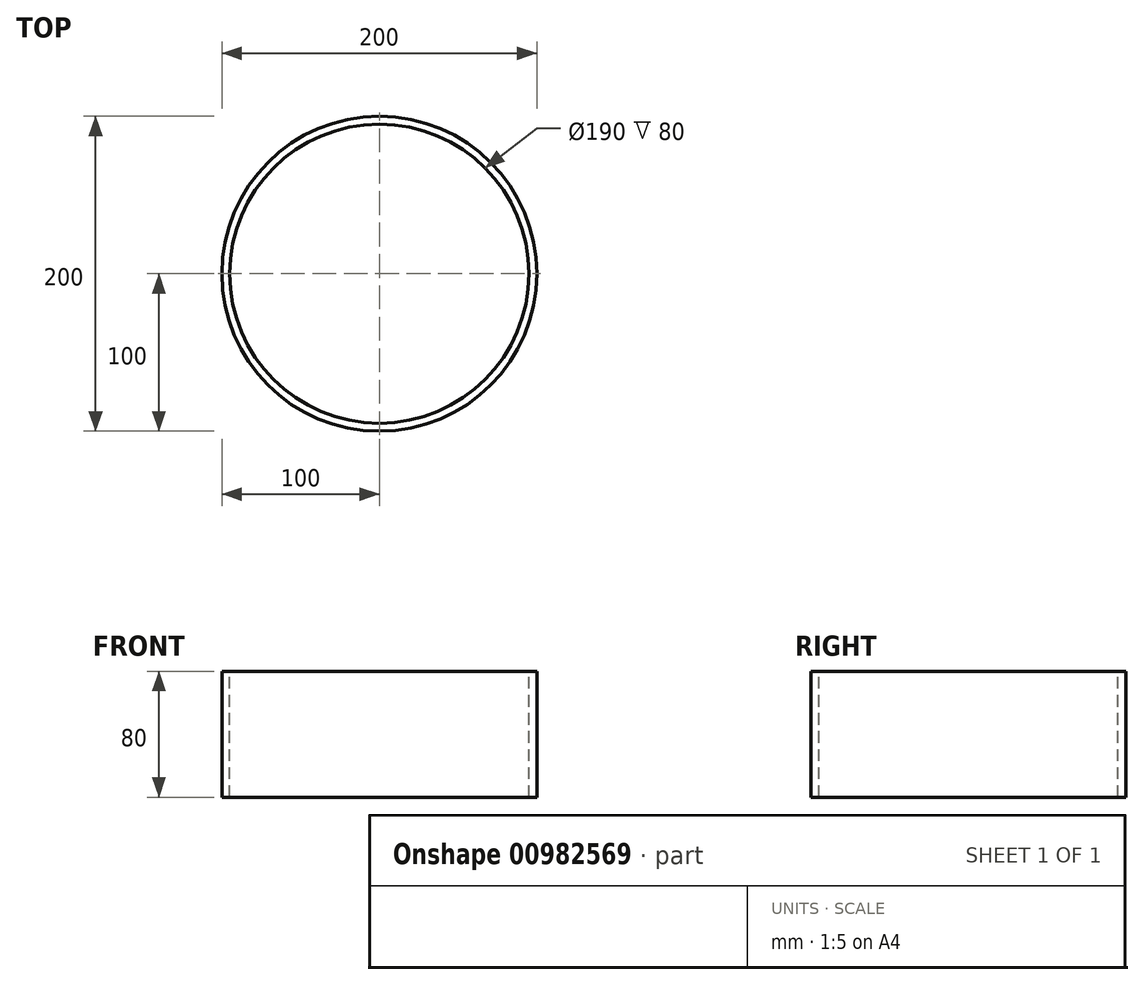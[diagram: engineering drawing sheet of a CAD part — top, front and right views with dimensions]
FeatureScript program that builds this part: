
annotation { "Feature Type Name" : "Feature", "Feature Type Description" : "" }
export const myFeature = defineFeature(function(context is Context, id is Id, definition is map)
    precondition{}
    {
        {
            var Q0;
            Q0=qCreatedBy(makeId("Top.planeOp"),FACE);
            var sketch = newSketch(context, id + "F0", { "sketchPlane" : qUnion([Q0])});
            skCircle(sketch, "E0", {"center": v(0, 0) * mm, "radius": 100 * mm});
            skCircle(sketch, "E1.0", {"center": v(0, 0) * mm, "radius": 95 * mm});
            skSolve(sketch);
        }
        {
            var Q0;
            Q0=qCreatedBy(makeId("Front.planeOp"),FACE);
            var sketch = newSketch(context, id + "F1", { "sketchPlane" : qUnion([Q0])});
            skLineSegment(sketch, "E2", {"start": v(0, 0) * mm, "end": v(0, 80) * mm});
            skSolve(sketch);
        }
        {
            var Q0;
            Q0=makeQuery(id+"F0.imprint","IMPRINT",FACE,{"disambiguationData":[TD([[makeQuery(id+"F0.imprint","IMPRINT",EDGE,{"derivedFrom":sQuery(id+"F0.wireOp",EDGE,"E0")}),1.0]])]});
            var Q1;
            Q1=sQuery(id+"F1.wireOp",EDGE,"E2");
            sweep(context, id + "F2", {"profiles" : qUnion([Q0]), "path" : qUnion([Q1])});
        }
    });
